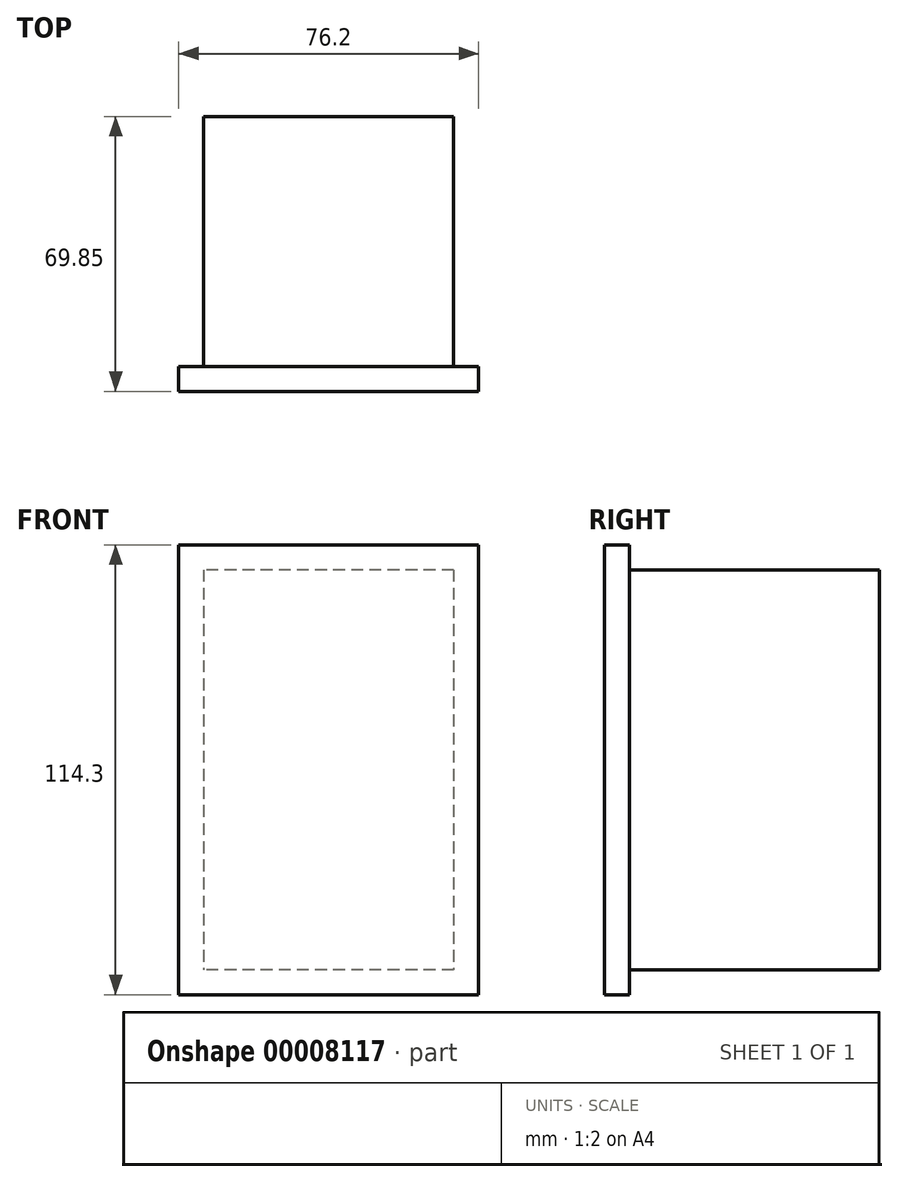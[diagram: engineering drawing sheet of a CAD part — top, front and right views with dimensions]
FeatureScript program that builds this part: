
annotation { "Feature Type Name" : "Feature", "Feature Type Description" : "" }
export const myFeature = defineFeature(function(context is Context, id is Id, definition is map)
    precondition{}
    {
        {
            var Q0;
            Q0=qCreatedBy(makeId("Front.planeOp"),FACE);
            var sketch = newSketch(context, id + "F0", { "sketchPlane" : qUnion([Q0])});
            skLineSegment(sketch, "E0.bottom", {"start": v(0, 114.3) * mm, "end": v(76.2, 114.3) * mm});
            skLineSegment(sketch, "E0.top", {"start": v(0, 0) * mm, "end": v(76.2, 0) * mm});
            skLineSegment(sketch, "E0.left", {"start": v(0, 114.3) * mm, "end": v(0, 0) * mm});
            skLineSegment(sketch, "E0.right", {"start": v(76.2, 114.3) * mm, "end": v(76.2, 0) * mm});
            skSolve(sketch);
        }
        {
            var Q0;
            Q0 = qSketchRegion(id + "F0", true);
            extrude(context, id + "F1", {"entities" : qUnion([Q0]), "depth" : 6.35 * mm});
        }
        {
            var Q0;
            Q0=makeQuery(id+"F1.opExtrude","CAP_FACE",FACE,{"disambiguationData":[OSD([sQuery(id+"F0.wireOp",EDGE,"E0.bottom"),sQuery(id+"F0.wireOp",EDGE,"E0.top"),sQuery(id+"F0.wireOp",EDGE,"E0.left"),sQuery(id+"F0.wireOp",EDGE,"E0.right")])],"isStart":true});
            var sketch = newSketch(context, id + "F2", { "sketchPlane" : qUnion([Q0])});
            skLineSegment(sketch, "E1.bottom", {"start": v(-69.85, 107.95) * mm, "end": v(-6.35, 107.95) * mm});
            skLineSegment(sketch, "E1.top", {"start": v(-69.85, 6.35) * mm, "end": v(-6.35, 6.35) * mm});
            skLineSegment(sketch, "E1.left", {"start": v(-69.85, 107.95) * mm, "end": v(-69.85, 6.35) * mm});
            skLineSegment(sketch, "E1.right", {"start": v(-6.35, 107.95) * mm, "end": v(-6.35, 6.35) * mm});
            skLineSegment(sketch, "E2", {"start": v(-38.1, 114.3) * mm, "end": v(-38.1, 107.95) * mm, "construction": true});
            skLineSegment(sketch, "E3", {"start": v(-76.2, 57.15) * mm, "end": v(-69.85, 57.15) * mm, "construction": true});
            skSolve(sketch);
        }
        {
            var Q0;
            Q0 = qSketchRegion(id + "F2", true);
            extrude(context, id + "F3", {"entities" : qUnion([Q0]), "operationType" : NewBodyOperationType.ADD, "depth" : 63.5 * mm});
        }
    });
